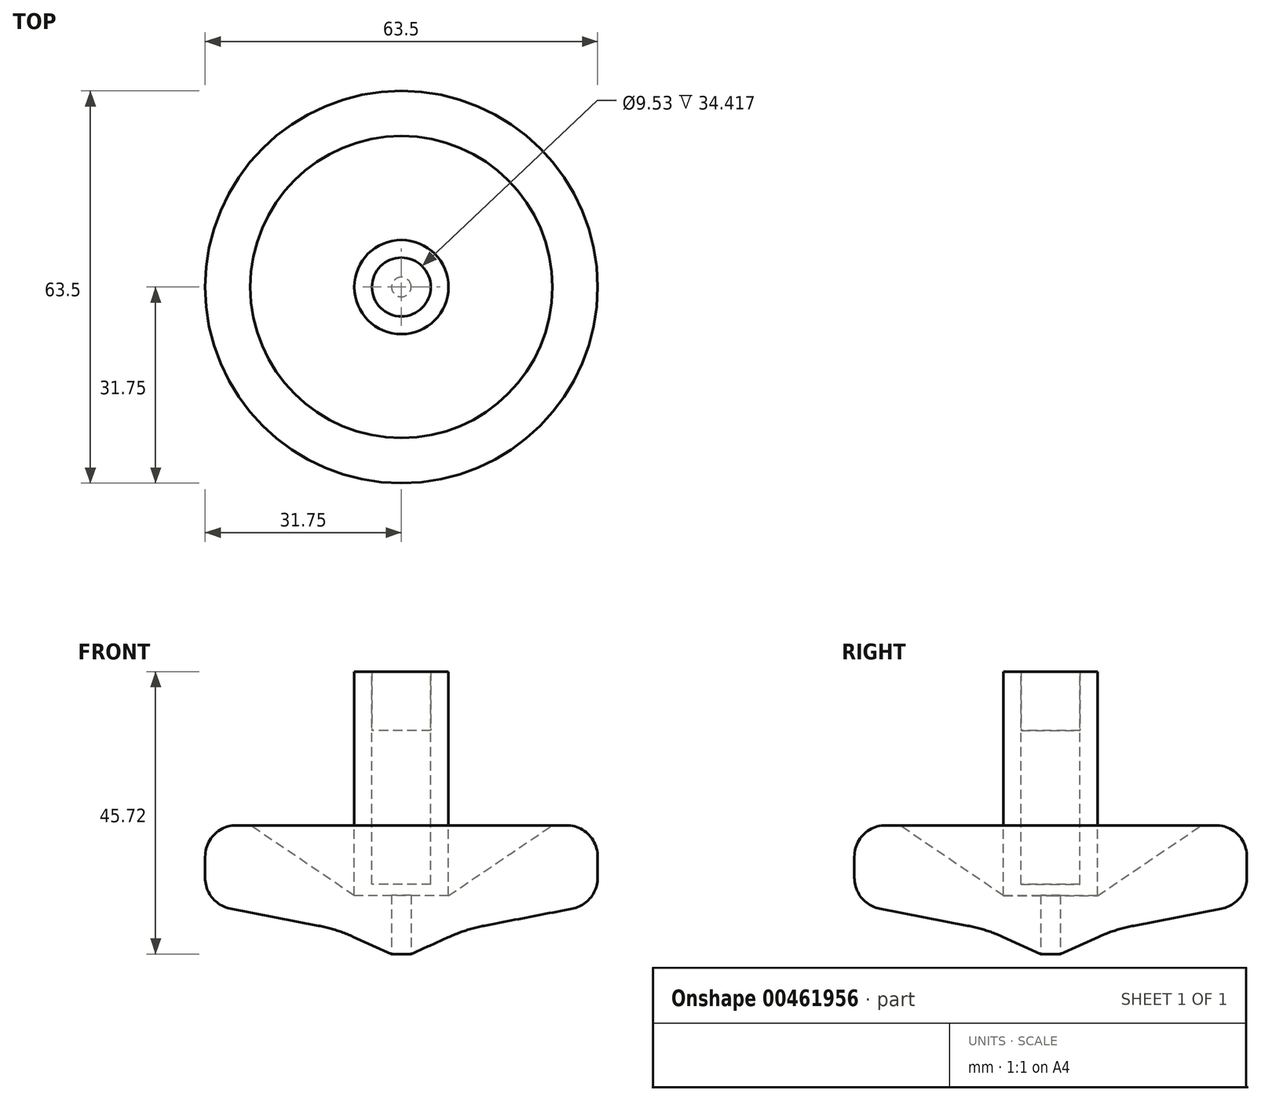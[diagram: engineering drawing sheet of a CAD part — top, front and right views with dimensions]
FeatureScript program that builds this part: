
annotation { "Feature Type Name" : "Feature", "Feature Type Description" : "" }
export const myFeature = defineFeature(function(context is Context, id is Id, definition is map)
    precondition{}
    {
        {
            var Q0;
            Q0=qCreatedBy(makeId("Front.planeOp"),FACE);
            var sketch = newSketch(context, id + "F0", { "sketchPlane" : qUnion([Q0])});
            skLineSegment(sketch, "E0", {"start": v(31.75, 8.13) * mm, "end": v(31.75, 20.83) * mm});
            skLineSegment(sketch, "E1", {"start": v(31.75, 20.83) * mm, "end": v(24.44, 20.83) * mm});
            skLineSegment(sketch, "E2", {"start": v(24.44, 20.83) * mm, "end": v(7.62, 9.44) * mm});
            skLineSegment(sketch, "E3", {"start": v(7.62, 9.44) * mm, "end": v(7.62, 45.72) * mm});
            skLineSegment(sketch, "E4", {"start": v(7.62, 45.72) * mm, "end": v(0, 45.72) * mm});
            skLineSegment(sketch, "E5", {"start": v(0, 45.72) * mm, "end": v(0, 0) * mm});
            skLineSegment(sketch, "E6", {"start": v(10.5, 4.02) * mm, "end": v(31.75, 8.13) * mm});
            skLineSegment(sketch, "E7", {"start": v(0, 0) * mm, "end": v(1.59, 0) * mm});
            skLineSegment(sketch, "E8", {"start": v(1.59, 0) * mm, "end": v(10.5, 4.02) * mm});
            skSolve(sketch);
        }
        {
            var Q0;
            Q0 = qSketchRegion(id + "F0", true);
            var Q1;
            Q1=sQuery(id+"F0.wireOp",EDGE,"E5");
            revolve(context, id + "F1", {"entities" : qUnion([Q0]), "axis" : qUnion([Q1]), "revolveType" : RevolveType.FULL});
        }
        {
            var Q0;
            Q0=makeQuery(id+"F1.opRevolve","SWEPT_FACE",FACE,{"disambiguationData":[OSD([sQuery(id+"F0.wireOp",EDGE,"E0")])]});
            fillet(context, id + "F2", {"entities" : qUnion([Q0]), "radius" : 5.08 * mm, "tangentPropagation" : true, "allowEdgeOverflow" : false});
        }
        {
            var Q0;
            Q0=makeQuery(id+"F1.opRevolve","SWEPT_EDGE",EDGE,{"disambiguationData":[OSD([sQuery(id+"F0.wireOp",EDGE,"E6"),sQuery(id+"F0.wireOp",EDGE,"E8")])]});
            fillet(context, id + "F3", {"entities" : qUnion([Q0]), "radius" : 25.4 * mm, "tangentPropagation" : true, "allowEdgeOverflow" : false});
        }
        {
            var Q0;
            Q0=makeQuery(id+"F1.opRevolve","SWEPT_FACE",FACE,{"disambiguationData":[OSD([sQuery(id+"F0.wireOp",EDGE,"E4")])]});
            var sketch = newSketch(context, id + "F4", { "sketchPlane" : qUnion([Q0])});
            skCircle(sketch, "E9", {"center": v(0, 0) * mm, "radius": 4.76 * mm});
            skSolve(sketch);
        }
        {
            var Q0;
            Q0 = qSketchRegion(id + "F4", true);
            extrude(context, id + "F5", {"entities" : qUnion([Q0]), "operationType" : NewBodyOperationType.REMOVE, "oppositeDirection" : true, "depth" : 9.52 * mm});
        }
        {
            var Q0;
            Q0=qCreatedBy(makeId("Top.planeOp"),FACE);
            var sketch = newSketch(context, id + "F6", { "sketchPlane" : qUnion([Q0])});
            skCircle(sketch, "E10", {"center": v(0, 0) * mm, "radius": 1.59 * mm});
            skSolve(sketch);
        }
        {
            var Q0;
            Q0 = qSketchRegion(id + "F6", true);
            extrude(context, id + "F7", {"entities" : qUnion([Q0]), "depth" : 9.52 * mm});
        }
        {
            var Q0;
            Q0=makeQuery(id+"F5.boolean.opBoolean","COPY",FACE,{"derivedFrom":makeQuery(id+"F5.opExtrude","CAP_FACE",FACE,{"disambiguationData":[OSD([sQuery(id+"F4.wireOp",EDGE,"E9")])],"isStart":false})});
            extrude(context, id + "F8", {"entities" : qUnion([Q0]), "depth" : 9.52 * mm});
        }
        {
            var Q0;
            Q0=makeQuery(id+"F5.boolean.opBoolean","COPY",FACE,{"derivedFrom":makeQuery(id+"F5.opExtrude","CAP_FACE",FACE,{"disambiguationData":[OSD([sQuery(id+"F4.wireOp",EDGE,"E9")])],"isStart":false})});
            extrude(context, id + "F9", {"entities" : qUnion([Q0]), "operationType" : NewBodyOperationType.REMOVE, "oppositeDirection" : true, "depth" : 24.9 * mm});
        }
    });
